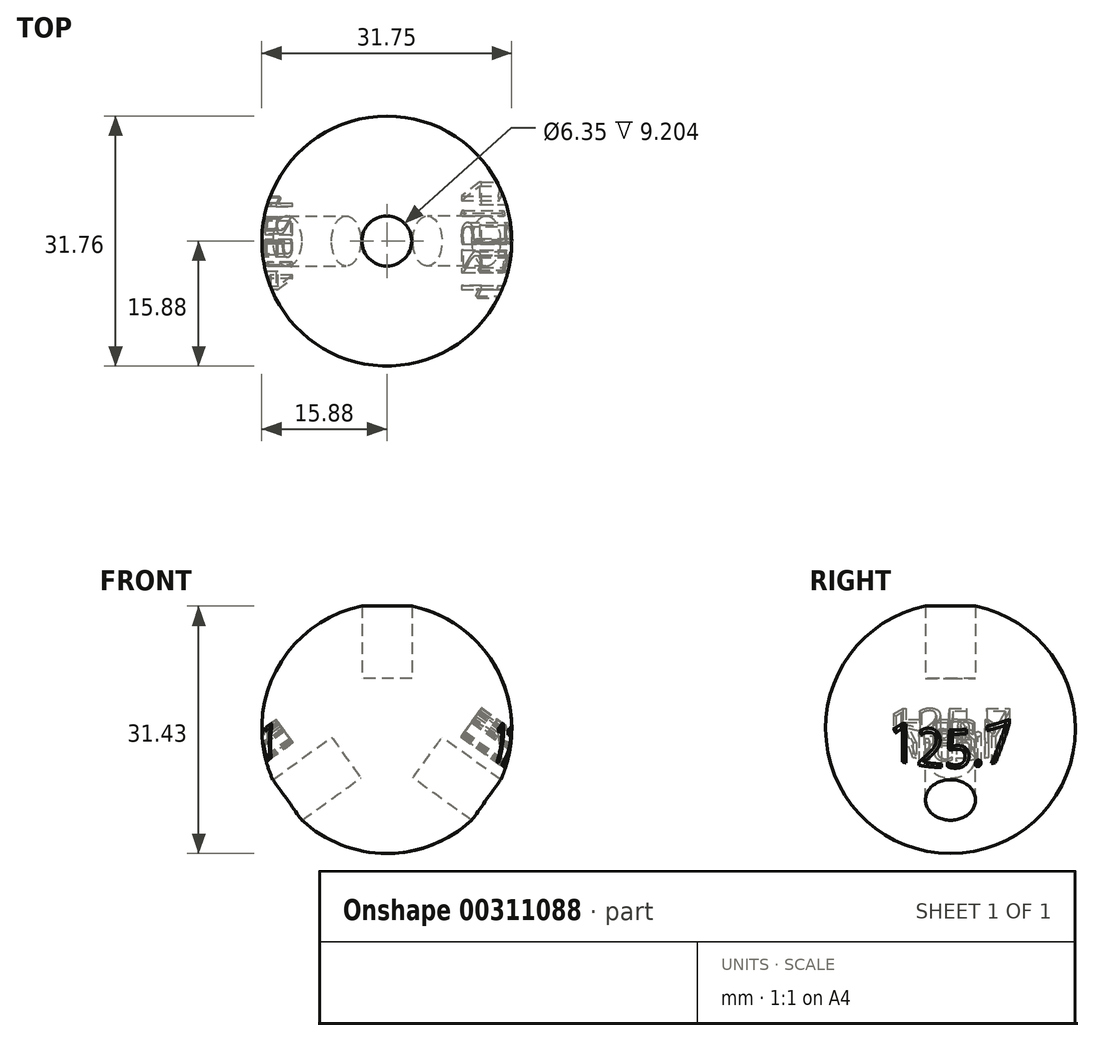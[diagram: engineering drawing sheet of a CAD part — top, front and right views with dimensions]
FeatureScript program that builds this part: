
annotation { "Feature Type Name" : "Feature", "Feature Type Description" : "" }
export const myFeature = defineFeature(function(context is Context, id is Id, definition is map)
    precondition{}
    {
        {
            var Q0;
            Q0=qCreatedBy(makeId("Front.planeOp"),FACE);
            var sketch = newSketch(context, id + "F0", { "sketchPlane" : qUnion([Q0])});
            skArc(sketch, "E0", {"start": v(0, 15.88) * mm, "mid": v(-15.88, 0) * mm, "end": v(0, -15.88) * mm});
            skLineSegment(sketch, "E1", {"start": v(0, 15.88) * mm, "end": v(0, -15.88) * mm});
            skSolve(sketch);
        }
        {
            var Q0;
            Q0=qCreatedBy(makeId("Top.planeOp"),FACE);
            var sketch = newSketch(context, id + "F1", { "sketchPlane" : qUnion([Q0])});
            skCircle(sketch, "E2", {"center": v(0, 0) * mm, "radius": 15.88 * mm});
            skSolve(sketch);
        }
        {
            var Q0;
            Q0=makeQuery(id+"F0.imprint","IMPRINT",FACE,{"disambiguationData":[TD([[makeQuery(id+"F0.imprint","IMPRINT",EDGE,{"derivedFrom":sQuery(id+"F0.wireOp",EDGE,"E0")}),1.0]])]});
            var Q1;
            Q1=sQuery(id+"F1.wireOp",EDGE,"E2");
            revolve(context, id + "F2", {"entities" : qUnion([Q0]), "axis" : qUnion([Q1]), "revolveType" : RevolveType.FULL});
        }
        {
            var Q0;
            Q0=qCreatedBy(makeId("Top.planeOp"),FACE);
            cPlane(context, id + "F3", {"entities" : qUnion([Q0]), "cplaneType" : CPlaneType.OFFSET, "offset" : 6.35 * mm, "width" : 152.4 * mm, "height" : 152.4 * mm});
        }
        {
            var Q0;
            Q0=qCreatedBy(id+"F3.planeOp",FACE);
            var sketch = newSketch(context, id + "F4", { "sketchPlane" : qUnion([Q0])});
            skCircle(sketch, "E3", {"center": v(0, 0) * mm, "radius": 3.18 * mm});
            skSolve(sketch);
        }
        {
            var Q0;
            Q0=makeQuery(id+"F4.imprint","IMPRINT",FACE,{"disambiguationData":[TD([[makeQuery(id+"F4.imprint","IMPRINT",EDGE,{"derivedFrom":sQuery(id+"F4.wireOp",EDGE,"E3")}),1.0]])]});
            extrude(context, id + "F5", {"entities" : qUnion([Q0]), "depth" : 50.8 * mm});
        }
        {
            var Q0;
            Q0=qCreatedBy(makeId("Top.planeOp"),FACE);
            var sketch = newSketch(context, id + "F6", { "sketchPlane" : qUnion([Q0])});
            skLineSegment(sketch, "E4", {"start": v(0, 0) * mm, "end": v(0, -74.85) * mm, "construction": true});
            skSolve(sketch);
        }
        {
            var Q0;
            Q0=makeQuery(id+"F5.opExtrude","SWEPT_BODY",BODY,{"disambiguationData":[OSD([sQuery(id+"F4.wireOp",EDGE,"E3")])]});
            var Q1;
            Q1=sQuery(id+"F6.wireOp",EDGE,"E4");
            transform(context, id + "F7", {"entities" : qUnion([Q0]), "transformType" : TransformType.ROTATION, "transformAxis" : qUnion([Q1]), "angle" : 125.7 * degree, "makeCopy" : true});
        }
        {
            var Q0;
            Q0=makeQuery(id+"F5.opExtrude","SWEPT_BODY",BODY,{"disambiguationData":[OSD([sQuery(id+"F4.wireOp",EDGE,"E3")])]});
            var Q1;
            Q1=sQuery(id+"F6.wireOp",EDGE,"E4");
            transform(context, id + "F8", {"entities" : qUnion([Q0]), "transformType" : TransformType.ROTATION, "transformAxis" : qUnion([Q1]), "angle" : 125.7 * degree, "oppositeDirection" : true, "makeCopy" : true});
        }
        {
            var Q0;
            Q0=makeQuery(id+"F8.opPattern","COPY",FACE,{"derivedFrom":makeQuery(id+"F5.opExtrude","CAP_FACE",FACE,{"disambiguationData":[OSD([sQuery(id+"F4.wireOp",EDGE,"E3")])],"isStart":false}),"instanceName":"1"});
            cPlane(context, id + "F9", {"entities" : qUnion([Q0]), "cplaneType" : CPlaneType.OFFSET, "offset" : 25.4 * mm, "oppositeDirection" : true, "width" : 152.4 * mm, "height" : 152.4 * mm});
        }
        {
            var Q0;
            Q0=qCreatedBy(id+"F9.planeOp",FACE);
            var sketch = newSketch(context, id + "F10", { "sketchPlane" : qUnion([Q0])});
            skText(sketch, "E5", { "text": "125.7\n", "fontName": "OpenSans-Regular.ttf"});
            const initialGuessF10  = {"E5": [-0.00779, 0.00474, 1, 0, 0.0044]};
            skSetInitialGuess(sketch, initialGuessF10);
            skSolve(sketch);
        }
        {
            var Q0;
            Q0 = qSketchRegion(id + "F10", true);
            extrude(context, id + "F11", {"entities" : qUnion([Q0]), "operationType" : NewBodyOperationType.REMOVE, "oppositeDirection" : true, "depth" : 23.47 * mm});
        }
        {
            var Q0;
            Q0=makeQuery(id+"F7.opPattern","COPY",FACE,{"derivedFrom":makeQuery(id+"F5.opExtrude","CAP_FACE",FACE,{"disambiguationData":[OSD([sQuery(id+"F4.wireOp",EDGE,"E3")])],"isStart":false}),"instanceName":"1"});
            cPlane(context, id + "F12", {"entities" : qUnion([Q0]), "cplaneType" : CPlaneType.OFFSET, "offset" : 25.4 * mm, "oppositeDirection" : true, "width" : 152.4 * mm, "height" : 152.4 * mm});
        }
        {
            var Q0;
            Q0=qCreatedBy(id+"F12.planeOp",FACE);
            var sketch = newSketch(context, id + "F13", { "sketchPlane" : qUnion([Q0])});
            skText(sketch, "E6", { "text": "125.7\n", "fontName": "OpenSans-Regular.ttf"});
            const initialGuessF13  = {"E6": [-0.00611, 0.00556, 1, 0, 0.00354]};
            skSetInitialGuess(sketch, initialGuessF13);
            skSolve(sketch);
        }
        {
            var Q0;
            Q0 = qSketchRegion(id + "F13", true);
            extrude(context, id + "F14", {"entities" : qUnion([Q0]), "operationType" : NewBodyOperationType.REMOVE, "oppositeDirection" : true, "depth" : 20.98 * mm});
        }
        {
            var Q0;
            Q0=makeQuery(id+"F5.opExtrude","SWEPT_BODY",BODY,{"disambiguationData":[OSD([sQuery(id+"F4.wireOp",EDGE,"E3")])]});
            var Q1;
            Q1=makeQuery(id+"F7.opPattern","COPY",BODY,{"derivedFrom":makeQuery(id+"F5.opExtrude","SWEPT_BODY",BODY,{"disambiguationData":[OSD([sQuery(id+"F4.wireOp",EDGE,"E3")])]}),"instanceName":"1"});
            var Q2;
            Q2=makeQuery(id+"F8.opPattern","COPY",BODY,{"derivedFrom":makeQuery(id+"F5.opExtrude","SWEPT_BODY",BODY,{"disambiguationData":[OSD([sQuery(id+"F4.wireOp",EDGE,"E3")])]}),"instanceName":"1"});
            var Q3;
            Q3=makeQuery(id+"F2.opRevolve","SWEPT_BODY",BODY,{"disambiguationData":[OSD([sQuery(id+"F0.wireOp",EDGE,"E0"),sQuery(id+"F0.wireOp",EDGE,"E1")])]});
            booleanBodies(context, id + "F15", {"operationType" : BooleanOperationType.SUBTRACTION, "tools" : qUnion([Q0, Q1, Q2]), "targets" : qUnion([Q3])});
        }
    });
